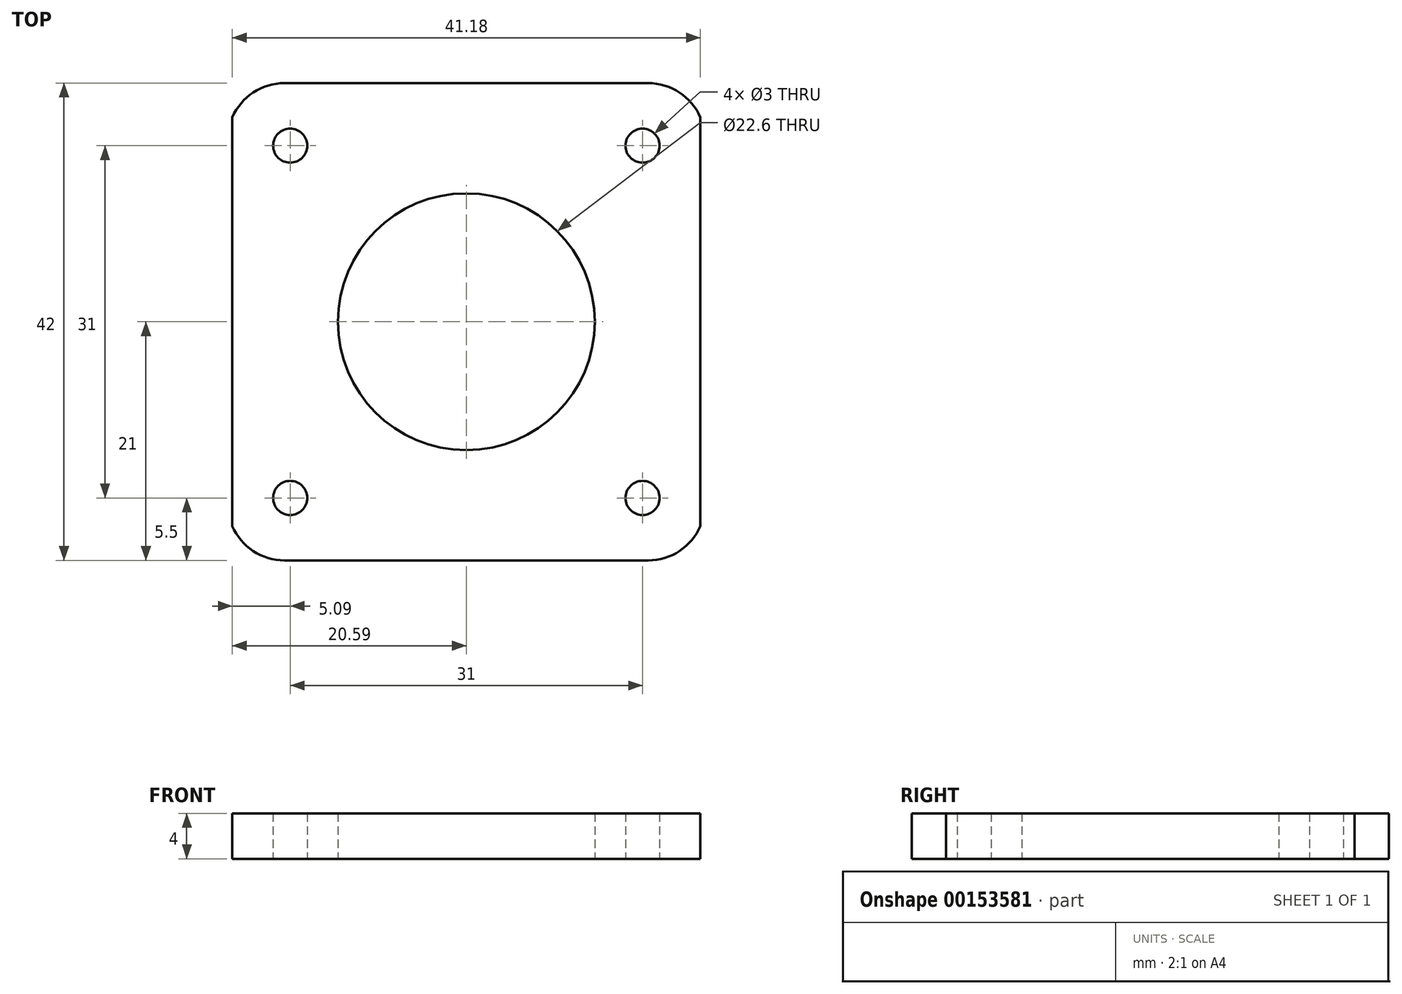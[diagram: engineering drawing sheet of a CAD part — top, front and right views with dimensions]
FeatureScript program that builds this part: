
annotation { "Feature Type Name" : "Feature", "Feature Type Description" : "" }
export const myFeature = defineFeature(function(context is Context, id is Id, definition is map)
    precondition{}
    {
        {
            var Q0;
            Q0=qCreatedBy(makeId("Top.planeOp"),FACE);
            var sketch = newSketch(context, id + "F0", { "sketchPlane" : qUnion([Q0])});
            skLineSegment(sketch, "E0.bottom", {"start": v(-15.5, 15.5) * mm, "end": v(15.5, 15.5) * mm, "construction": true});
            skLineSegment(sketch, "E0.top", {"start": v(-15.5, -15.5) * mm, "end": v(15.5, -15.5) * mm, "construction": true});
            skLineSegment(sketch, "E0.left", {"start": v(-15.5, 15.5) * mm, "end": v(-15.5, -15.5) * mm, "construction": true});
            skLineSegment(sketch, "E0.right", {"start": v(15.5, 15.5) * mm, "end": v(15.5, -15.5) * mm, "construction": true});
            skPoint(sketch, "E0.middle", {"position": v(0, 0) * mm});
            skCircle(sketch, "E1", {"center": v(-15.5, 15.5) * mm, "radius": 1.5 * mm});
            skCircle(sketch, "E2", {"center": v(15.5, 15.5) * mm, "radius": 1.5 * mm});
            skCircle(sketch, "E3", {"center": v(15.5, -15.5) * mm, "radius": 1.5 * mm});
            skCircle(sketch, "E4", {"center": v(-15.5, -15.5) * mm, "radius": 1.5 * mm});
            skCircle(sketch, "E5", {"center": v(0, 0) * mm, "radius": 11.3 * mm});
            skPoint(sketch, "E6.visualSharp", {"position": v(-21, -21) * mm});
            skPoint(sketch, "E7.visualSharp", {"position": v(21, -21) * mm});
            skLineSegment(sketch, "E8.bottom", {"start": v(-16, 21) * mm, "end": v(16, 21) * mm});
            skLineSegment(sketch, "E8.top", {"start": v(-16, -21) * mm, "end": v(16, -21) * mm});
            skPoint(sketch, "E9.visualSharp", {"position": v(-21, 21) * mm});
            skArc(sketch, "E9.filletArc", {"start": v(-16, 21) * mm, "mid": v(-18.75, 20.18) * mm, "end": v(-20.6, 17.98) * mm});
            skPoint(sketch, "E10.visualSharp", {"position": v(21, 21) * mm});
            skArc(sketch, "E10.filletArc", {"start": v(20.6, 17.98) * mm, "mid": v(18.75, 20.18) * mm, "end": v(16, 21) * mm});
            skArc(sketch, "E11.filletArc", {"start": v(16, -21) * mm, "mid": v(18.75, -20.18) * mm, "end": v(20.6, -17.98) * mm});
            skArc(sketch, "E12.filletArc", {"start": v(-20.6, -17.98) * mm, "mid": v(-18.75, -20.18) * mm, "end": v(-16, -21) * mm});
            skLineSegment(sketch, "E13", {"start": v(-20.6, 17.98) * mm, "end": v(-20.6, -17.98) * mm});
            skLineSegment(sketch, "E14", {"start": v(20.6, 17.98) * mm, "end": v(20.6, -17.98) * mm});
            skSolve(sketch);
        }
        {
            var Q0;
            Q0=makeQuery(id+"F0.imprint","IMPRINT",FACE,{"disambiguationData":[TD([[makeQuery(id+"F0.imprint","IMPRINT",EDGE,{"derivedFrom":sQuery(id+"F0.wireOp",EDGE,"E1")}),-1.0]])]});
            extrude(context, id + "F1", {"entities" : qUnion([Q0]), "depth" : 4 * mm});
        }
    });
